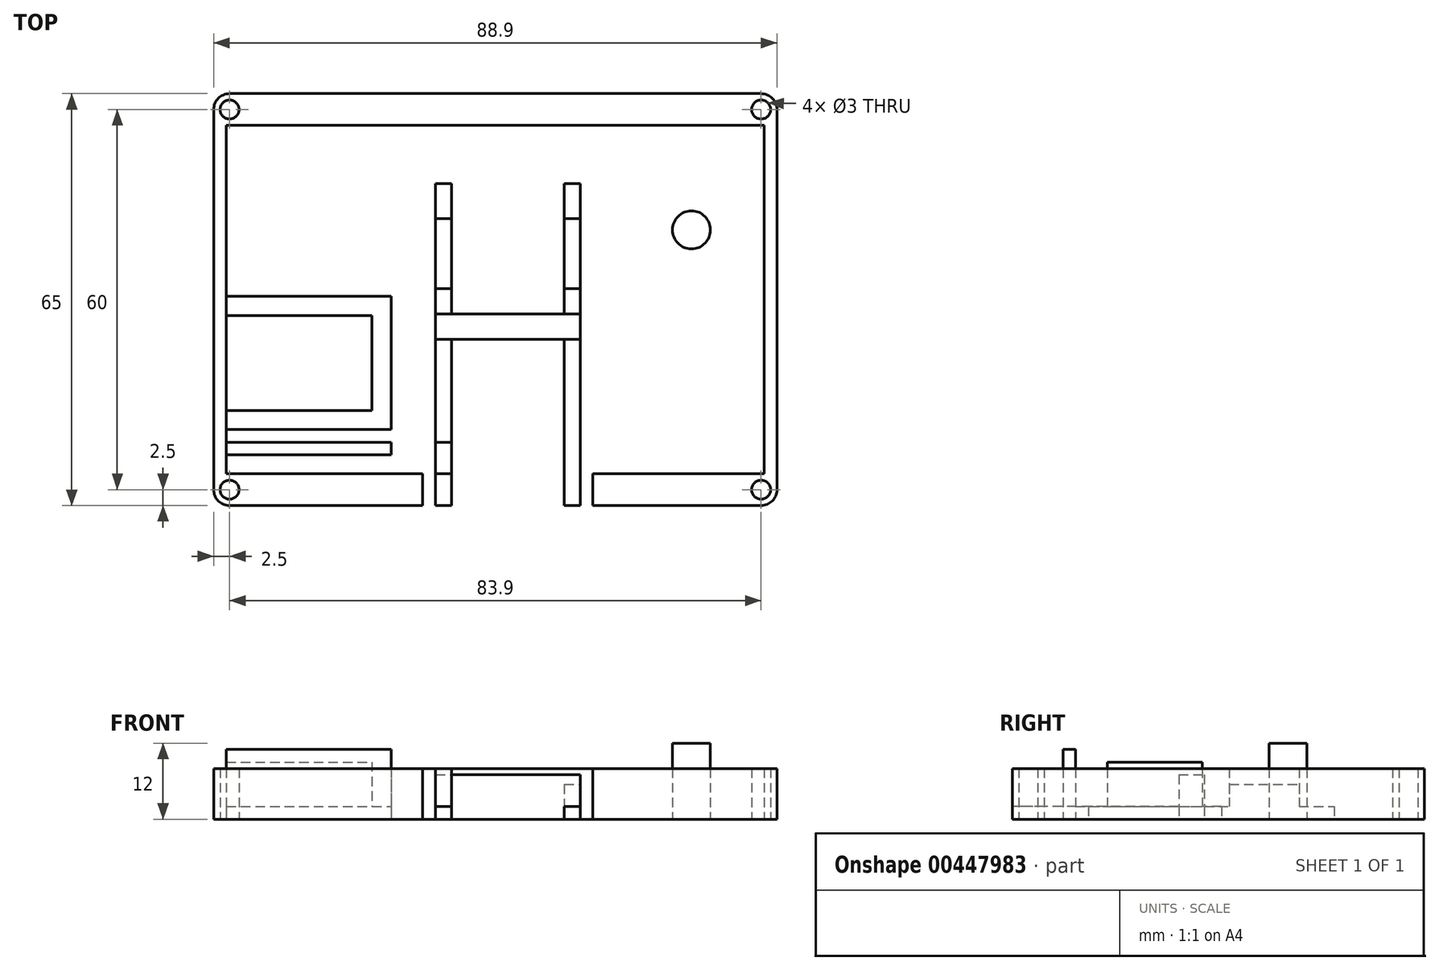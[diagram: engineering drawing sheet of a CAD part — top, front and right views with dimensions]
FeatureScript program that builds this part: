
annotation { "Feature Type Name" : "Feature", "Feature Type Description" : "" }
export const myFeature = defineFeature(function(context is Context, id is Id, definition is map)
    precondition{}
    {
        {
            var Q0;
            Q0=qCreatedBy(makeId("Top.planeOp"),FACE);
            var sketch = newSketch(context, id + "F0", { "sketchPlane" : qUnion([Q0])});
            skLineSegment(sketch, "E0.top", {"start": v(42.45, 27.5) * mm, "end": v(-42.45, 27.5) * mm});
            skLineSegment(sketch, "E0.left", {"start": v(44.45, -27.5) * mm, "end": v(44.45, 27.5) * mm});
            skLineSegment(sketch, "E0.right", {"start": v(-44.45, -27.5) * mm, "end": v(-44.45, 27.5) * mm});
            skPoint(sketch, "E0.middle", {"position": v(0, 0) * mm});
            skLineSegment(sketch, "E1", {"start": v(42.45, 31.41) * mm, "end": v(42.45, 31.27) * mm, "construction": true});
            skLineSegment(sketch, "E2.left", {"start": v(42.45, -20.5) * mm, "end": v(42.45, 0.5) * mm});
            skLineSegment(sketch, "E3.bottom", {"start": v(-42.45, 27.5) * mm, "end": v(42.45, 27.5) * mm});
            skLineSegment(sketch, "E3.top", {"start": v(-41.95, 32.5) * mm, "end": v(41.95, 32.5) * mm});
            skLineSegment(sketch, "E3.left", {"start": v(-44.45, 27.5) * mm, "end": v(-44.45, 30) * mm});
            skLineSegment(sketch, "E3.right", {"start": v(44.45, 27.5) * mm, "end": v(44.45, 30) * mm});
            skLineSegment(sketch, "E4.top", {"start": v(-41.95, -32.5) * mm, "end": v(41.95, -32.5) * mm});
            skLineSegment(sketch, "E4.left", {"start": v(-44.45, -27.5) * mm, "end": v(-44.45, -30) * mm});
            skLineSegment(sketch, "E4.right", {"start": v(44.45, -27.5) * mm, "end": v(44.45, -30) * mm});
            skPoint(sketch, "E5.visualSharp", {"position": v(-44.45, 32.5) * mm});
            skArc(sketch, "E5.filletArc", {"start": v(-41.95, 32.5) * mm, "mid": v(-43.72, 31.77) * mm, "end": v(-44.45, 30) * mm});
            skPoint(sketch, "E6.visualSharp", {"position": v(44.45, 32.5) * mm});
            skArc(sketch, "E6.filletArc", {"start": v(44.45, 30) * mm, "mid": v(43.72, 31.77) * mm, "end": v(41.95, 32.5) * mm});
            skPoint(sketch, "E7.visualSharp", {"position": v(44.45, -32.5) * mm});
            skArc(sketch, "E7.filletArc", {"start": v(41.95, -32.5) * mm, "mid": v(43.72, -31.77) * mm, "end": v(44.45, -30) * mm});
            skPoint(sketch, "E8.visualSharp", {"position": v(-44.45, -32.5) * mm});
            skArc(sketch, "E8.filletArc", {"start": v(-44.45, -30) * mm, "mid": v(-43.72, -31.77) * mm, "end": v(-41.95, -32.5) * mm});
            skCircle(sketch, "E9", {"center": v(-41.95, 30) * mm, "radius": 1.5 * mm});
            skCircle(sketch, "E10", {"center": v(41.95, 30) * mm, "radius": 1.5 * mm});
            skCircle(sketch, "E11", {"center": v(-41.95, -30) * mm, "radius": 1.5 * mm});
            skCircle(sketch, "E12", {"center": v(41.95, -30) * mm, "radius": 1.5 * mm});
            skLineSegment(sketch, "E13.trimOffspring", {"start": v(42.45, 0.5) * mm, "end": v(42.45, -20.5) * mm, "construction": true});
            skLineSegment(sketch, "E14.trimOffspring", {"start": v(42.45, -32.45) * mm, "end": v(42.45, -32.5) * mm, "construction": true});
            skPoint(sketch, "E0.bottom.end.orphan", {"position": v(9.45, -27.5) * mm});
            skLineSegment(sketch, "E15.bottom", {"start": v(-9.45, -32.5) * mm, "end": v(13.41, -32.5) * mm});
            skLineSegment(sketch, "E15.top", {"start": v(-9.45, 18.3) * mm, "end": v(13.4, 18.3) * mm});
            skLineSegment(sketch, "E15.left", {"start": v(-9.45, -32.5) * mm, "end": v(-9.45, 18.3) * mm});
            skLineSegment(sketch, "E15.right", {"start": v(13.41, -32.5) * mm, "end": v(13.4, 18.3) * mm});
            skLineSegment(sketch, "E16.0", {"start": v(10.87, -29.96) * mm, "end": v(10.87, 15.76) * mm});
            skLineSegment(sketch, "E16.1", {"start": v(-6.91, 15.76) * mm, "end": v(10.87, 15.76) * mm, "construction": true});
            skLineSegment(sketch, "E16.2", {"start": v(-6.9, -29.96) * mm, "end": v(-6.91, 15.76) * mm});
            skLineSegment(sketch, "E17", {"start": v(-6.9, -29.96) * mm, "end": v(10.87, -29.96) * mm, "construction": true});
            skLineSegment(sketch, "E18", {"start": v(-42.45, -27.5) * mm, "end": v(-11.45, -27.5) * mm});
            skLineSegment(sketch, "E19", {"start": v(15.41, -27.5) * mm, "end": v(42.45, -27.5) * mm});
            skLineSegment(sketch, "E20", {"start": v(42.45, 27.5) * mm, "end": v(42.45, -27.5) * mm});
            skLineSegment(sketch, "E21", {"start": v(-42.45, 27.5) * mm, "end": v(-42.45, -27.5) * mm});
            skLineSegment(sketch, "E22", {"start": v(-11.45, -27.5) * mm, "end": v(-11.45, -32.5) * mm});
            skLineSegment(sketch, "E23", {"start": v(15.41, -27.5) * mm, "end": v(15.41, -32.5) * mm});
            skPoint(sketch, "E24.MirrorP", {"position": v(30.95, 11) * mm});
            skLineSegment(sketch, "E25.MirrorCS", {"start": v(-42.45, 0.5) * mm, "end": v(-16.45, 0.5) * mm});
            skLineSegment(sketch, "E26.MirrorCS", {"start": v(-16.45, -20.5) * mm, "end": v(-16.45, 0.5) * mm});
            skLineSegment(sketch, "E27.MirrorCS", {"start": v(-42.45, -20.5) * mm, "end": v(-16.45, -20.5) * mm});
            skCircle(sketch, "E28", {"center": v(30.95, 11) * mm, "radius": 3 * mm});
            skLineSegment(sketch, "E29.0", {"start": v(-42.45, -17.5) * mm, "end": v(-19.45, -17.5) * mm});
            skLineSegment(sketch, "E29.1", {"start": v(-19.45, -17.5) * mm, "end": v(-19.45, -2.5) * mm});
            skLineSegment(sketch, "E29.2", {"start": v(-42.45, -2.5) * mm, "end": v(-19.45, -2.5) * mm});
            skLineSegment(sketch, "E30", {"start": v(-42.45, 2.5) * mm, "end": v(-16.5, 2.5) * mm});
            skLineSegment(sketch, "E31", {"start": v(-42.45, -22.5) * mm, "end": v(-16.5, -22.5) * mm});
            skLineSegment(sketch, "E32.bottom", {"start": v(-42.45, -22.5) * mm, "end": v(-16.42, -22.5) * mm});
            skLineSegment(sketch, "E32.top", {"start": v(-42.45, -24.5) * mm, "end": v(-16.42, -24.5) * mm});
            skLineSegment(sketch, "E32.left", {"start": v(-42.45, -22.5) * mm, "end": v(-42.45, -24.5) * mm});
            skLineSegment(sketch, "E32.right", {"start": v(-16.42, -22.5) * mm, "end": v(-16.42, -24.5) * mm});
            skLineSegment(sketch, "E33.left", {"start": v(-42.45, 2.5) * mm, "end": v(-42.45, 2.5) * mm});
            skLineSegment(sketch, "E33.right", {"start": v(-16.5, 2.5) * mm, "end": v(-16.5, 2.5) * mm});
            skLineSegment(sketch, "E34.bottom", {"start": v(-16.5, 2.5) * mm, "end": v(-42.45, 2.5) * mm});
            skLineSegment(sketch, "E34.top", {"start": v(-16.5, 4.5) * mm, "end": v(-42.45, 4.5) * mm});
            skLineSegment(sketch, "E34.left", {"start": v(-16.5, 2.5) * mm, "end": v(-16.5, 4.5) * mm});
            skLineSegment(sketch, "E34.right", {"start": v(-42.45, 2.5) * mm, "end": v(-42.45, 4.5) * mm});
            skLineSegment(sketch, "E35", {"start": v(-9.45, -2.24) * mm, "end": v(13.41, -2.24) * mm});
            skLineSegment(sketch, "E36", {"start": v(-9.45, -6.24) * mm, "end": v(13.41, -6.24) * mm});
            skLineSegment(sketch, "E37", {"start": v(-9.45, 12.76) * mm, "end": v(-6.91, 12.76) * mm});
            skLineSegment(sketch, "E38", {"start": v(-9.45, 1.76) * mm, "end": v(-6.91, 1.76) * mm});
            skLineSegment(sketch, "E39", {"start": v(-9.45, -27.5) * mm, "end": v(-6.9, -27.5) * mm});
            skLineSegment(sketch, "E40", {"start": v(-9.45, -22.5) * mm, "end": v(-6.9, -22.5) * mm});
            skLineSegment(sketch, "E41", {"start": v(-6.9, -22.5) * mm, "end": v(-6.9, -27.5) * mm});
            skLineSegment(sketch, "E42", {"start": v(-6.91, 12.76) * mm, "end": v(-6.91, 1.76) * mm});
            skLineSegment(sketch, "E43", {"start": v(-6.91, 15.76) * mm, "end": v(-6.91, 18.3) * mm});
            skLineSegment(sketch, "E44", {"start": v(10.87, 15.76) * mm, "end": v(10.87, 18.3) * mm});
            skLineSegment(sketch, "E45", {"start": v(-6.9, -29.96) * mm, "end": v(-6.9, -32.5) * mm});
            skLineSegment(sketch, "E46", {"start": v(10.87, -29.96) * mm, "end": v(10.87, -32.5) * mm});
            skLineSegment(sketch, "E47", {"start": v(10.87, 12.76) * mm, "end": v(13.4, 12.76) * mm});
            skLineSegment(sketch, "E48", {"start": v(10.87, 1.76) * mm, "end": v(13.4, 1.76) * mm});
            skLineSegment(sketch, "E49.bottom", {"start": v(-6.91, 18.3) * mm, "end": v(10.87, 18.3) * mm});
            skLineSegment(sketch, "E49.top", {"start": v(-6.91, 18.3) * mm, "end": v(10.87, 18.3) * mm});
            skLineSegment(sketch, "E49.left", {"start": v(-6.91, 18.3) * mm, "end": v(-6.91, 18.3) * mm});
            skLineSegment(sketch, "E49.right", {"start": v(10.87, 18.3) * mm, "end": v(10.87, 18.3) * mm});
            skLineSegment(sketch, "E50.top", {"start": v(-6.91, 19.3) * mm, "end": v(10.87, 19.3) * mm});
            skLineSegment(sketch, "E50.left", {"start": v(-6.91, 18.3) * mm, "end": v(-6.91, 19.3) * mm});
            skLineSegment(sketch, "E50.right", {"start": v(10.87, 18.3) * mm, "end": v(10.87, 19.3) * mm});
            skSolve(sketch);
        }
        {
            var Q0;
            Q0=makeQuery(id+"F0.imprint","IMPRINT",FACE,{"disambiguationData":[TD([[makeQuery(id+"F0.imprint","IMPRINT",EDGE,{"derivedFrom":sQuery(id+"F0.wireOp",EDGE,"b49GfUds-FCf6-TdCI-vDs9-xqUNhDrC5P7H")}),1.0]])]});
            var Q1;
            Q1=makeQuery(id+"F0.imprint","IMPRINT",FACE,{"disambiguationData":[TD([[makeQuery(id+"F0.imprint","IMPRINT",EDGE,{"derivedFrom":sQuery(id+"F0.wireOp",EDGE,"zLugwVok-1eod-zGnS-IKgy-gRwgS7il9mY1")}),1.0]])]});
            var Q2;
            Q2=makeQuery(id+"F0.imprint","IMPRINT",FACE,{"disambiguationData":[TD([[makeQuery(id+"F0.imprint","IMPRINT",EDGE,{"derivedFrom":sQuery(id+"F0.wireOp",EDGE,"gfQSOBsQ-dL06-kA9A-z0KN-fCnpzNCFb0XH")}),1.0]])]});
            var Q3;
            Q3=makeQuery(id+"F0.imprint","IMPRINT",FACE,{"disambiguationData":[TD([[makeQuery(id+"F0.imprint","IMPRINT",EDGE,{"derivedFrom":sQuery(id+"F0.wireOp",EDGE,"Z4DMVKM8-imfN-ioXY-uNkh-o1IQfbVLOKmH")}),1.0]])]});
            var Q4;
            Q4=makeQuery(id+"F0.imprint","IMPRINT",FACE,{"disambiguationData":[TD([[makeQuery(id+"F0.imprint","IMPRINT",EDGE,{"derivedFrom":sQuery(id+"F0.wireOp",EDGE,"E0.left")}),1.0]])]});
            var Q5;
            {var subQ0=sQuery(id+"F0.wireOp",EDGE,"5yO6ONQU-jHeC-KW85-spt1-Q7ioaqvRXlnz");Q5=makeQuery(id+"F0.imprint","IMPRINT",FACE,{"disambiguationData":[TD([[makeQuery(id+"F0.imprint","IMPRINT",EDGE,{"derivedFrom":subQ0}),-1.0]])]});}
            var Q6;
            {var subQ0=sQuery(id+"F0.wireOp",EDGE,"J2lE2n3h-ec9A-8HLJ-wN6o-8rqhVOWuaEZe");Q6=makeQuery(id+"F0.imprint","IMPRINT",FACE,{"disambiguationData":[TD([[makeQuery(id+"F0.imprint","IMPRINT",EDGE,{"derivedFrom":subQ0}),-1.0]])]});}
            var Q7;
            {var subQ0=sQuery(id+"F0.wireOp",EDGE,"E37");Q7=makeQuery(id+"F0.imprint","IMPRINT",FACE,{"disambiguationData":[TD([[makeQuery(id+"F0.imprint","IMPRINT",EDGE,{"derivedFrom":subQ0}),-1.0]])]});}
            var Q8;
            {var subQ0=sQuery(id+"F0.wireOp",EDGE,"E39");Q8=makeQuery(id+"F0.imprint","IMPRINT",FACE,{"disambiguationData":[TD([[makeQuery(id+"F0.imprint","IMPRINT",EDGE,{"derivedFrom":subQ0}),1.0]])]});}
            extrude(context, id + "F1", {"entities" : qUnion([Q0, Q1, Q2, Q3, Q4, Q5, Q6, Q7, Q8]), "depth" : 8 * mm});
        }
        {
            var Q0;
            {var subQ3=sQuery(id+"F0.wireOp",EDGE,"E3.bottom");Q0=makeQuery(id+"F0.imprint","IMPRINT",FACE,{"disambiguationData":[TD([[makeQuery(id+"F0.imprint","IMPRINT",EDGE,{"derivedFrom":subQ3}),-1.0]])]});}
            var Q1;
            {var subQ0=sQuery(id+"F0.wireOp",EDGE,"E25.MirrorCS");Q1=makeQuery(id+"F0.imprint","IMPRINT",FACE,{"disambiguationData":[TD([[makeQuery(id+"F0.imprint","IMPRINT",EDGE,{"derivedFrom":subQ0}),-1.0]])]});}
            var Q2;
            {var subQ3=sQuery(id+"F0.wireOp",EDGE,"E40");Q2=makeQuery(id+"F0.imprint","IMPRINT",FACE,{"disambiguationData":[TD([[makeQuery(id+"F0.imprint","IMPRINT",EDGE,{"derivedFrom":subQ3}),1.0]])]});}
            var Q3;
            {var subQ0=sQuery(id+"F0.wireOp",EDGE,"E35");var subQ1=sQuery(id+"F0.wireOp",EDGE,"E15.left");var subQ2=makeQuery(id+"F0.imprint","INTERSECT",VERTEX,{"derivedFrom":[subQ1,subQ0]});Q3=makeQuery(id+"F0.imprint","IMPRINT",FACE,{"disambiguationData":[TD([[makeQuery(id+"F0.imprint","IMPRINT",EDGE,{"disambiguationData":[TD([[subQ2,1.0]])],"derivedFrom":subQ1}),-1.0]])]});}
            var Q4;
            {var subQ3=sQuery(id+"F0.wireOp",EDGE,"E38");Q4=makeQuery(id+"F0.imprint","IMPRINT",FACE,{"disambiguationData":[TD([[makeQuery(id+"F0.imprint","IMPRINT",EDGE,{"derivedFrom":subQ3}),-1.0]])]});}
            var Q5;
            {var subQ0=sQuery(id+"F0.wireOp",EDGE,"E37");Q5=makeQuery(id+"F0.imprint","IMPRINT",FACE,{"disambiguationData":[TD([[makeQuery(id+"F0.imprint","IMPRINT",EDGE,{"derivedFrom":subQ0}),1.0]])]});}
            var Q6;
            {var subQ0=sQuery(id+"F0.wireOp",EDGE,"E39");Q6=makeQuery(id+"F0.imprint","IMPRINT",FACE,{"disambiguationData":[TD([[makeQuery(id+"F0.imprint","IMPRINT",EDGE,{"derivedFrom":subQ0}),-1.0]])]});}
            var Q7;
            {var subQ5=sQuery(id+"F0.wireOp",EDGE,"E46");Q7=makeQuery(id+"F0.imprint","IMPRINT",FACE,{"disambiguationData":[TD([[makeQuery(id+"F0.imprint","IMPRINT",EDGE,{"derivedFrom":subQ5}),1.0]])]});}
            var Q8;
            {var subQ0=sQuery(id+"F0.wireOp",EDGE,"E35");var subQ1=sQuery(id+"F0.wireOp",EDGE,"E15.right");var subQ2=makeQuery(id+"F0.imprint","INTERSECT",VERTEX,{"derivedFrom":[subQ1,subQ0]});Q8=makeQuery(id+"F0.imprint","IMPRINT",FACE,{"disambiguationData":[TD([[makeQuery(id+"F0.imprint","IMPRINT",EDGE,{"disambiguationData":[TD([[subQ2,1.0]])],"derivedFrom":subQ1}),1.0]])]});}
            var Q9;
            {var subQ5=sQuery(id+"F0.wireOp",EDGE,"E44");Q9=makeQuery(id+"F0.imprint","IMPRINT",FACE,{"disambiguationData":[TD([[makeQuery(id+"F0.imprint","IMPRINT",EDGE,{"derivedFrom":subQ5}),-1.0]])]});}
            var Q10;
            {var subQ3=sQuery(id+"F0.wireOp",EDGE,"E48");Q10=makeQuery(id+"F0.imprint","IMPRINT",FACE,{"disambiguationData":[TD([[makeQuery(id+"F0.imprint","IMPRINT",EDGE,{"derivedFrom":subQ3}),-1.0]])]});}
            extrude(context, id + "F2", {"entities" : qUnion([Q0, Q1, Q2, Q3, Q4, Q5, Q6, Q7, Q8, Q9, Q10]), "operationType" : NewBodyOperationType.ADD, "depth" : 2 * mm});
        }
        {
            var Q0;
            {var subQ0=sQuery(id+"F0.wireOp",EDGE,"E29.0");Q0=makeQuery(id+"F0.imprint","IMPRINT",FACE,{"disambiguationData":[TD([[makeQuery(id+"F0.imprint","IMPRINT",EDGE,{"derivedFrom":subQ0}),1.0]])]});}
            extrude(context, id + "F3", {"entities" : qUnion([Q0]), "operationType" : NewBodyOperationType.ADD, "depth" : 9 * mm});
        }
        {
            var Q0;
            Q0=makeQuery(id+"F0.imprint","IMPRINT",FACE,{"disambiguationData":[TD([[makeQuery(id+"F0.imprint","IMPRINT",EDGE,{"derivedFrom":sQuery(id+"F0.wireOp",EDGE,"E34.bottom")}),-1.0]])]});
            var Q1;
            Q1=makeQuery(id+"F0.imprint","IMPRINT",FACE,{"disambiguationData":[TD([[makeQuery(id+"F0.imprint","IMPRINT",EDGE,{"derivedFrom":sQuery(id+"F0.wireOp",EDGE,"E32.top")}),1.0]])]});
            extrude(context, id + "F4", {"entities" : qUnion([Q0, Q1]), "operationType" : NewBodyOperationType.ADD, "depth" : 11 * mm});
        }
        {
            var Q0;
            {var subQ0=sQuery(id+"F0.wireOp",EDGE,"E36");var subQ1=sQuery(id+"F0.wireOp",EDGE,"E16.0");var subQ2=makeQuery(id+"F0.imprint","INTERSECT",VERTEX,{"derivedFrom":[subQ1,subQ0]});Q0=makeQuery(id+"F0.imprint","IMPRINT",FACE,{"disambiguationData":[TD([[makeQuery(id+"F0.imprint","IMPRINT",EDGE,{"disambiguationData":[TD([[subQ2,-1.0]])],"derivedFrom":subQ1}),1.0]])]});}
            var Q1;
            {var subQ0=sQuery(id+"F0.wireOp",EDGE,"E35");var subQ1=sQuery(id+"F0.wireOp",EDGE,"E15.right");var subQ2=makeQuery(id+"F0.imprint","INTERSECT",VERTEX,{"derivedFrom":[subQ1,subQ0]});Q1=makeQuery(id+"F0.imprint","IMPRINT",FACE,{"disambiguationData":[TD([[makeQuery(id+"F0.imprint","IMPRINT",EDGE,{"disambiguationData":[TD([[subQ2,1.0]])],"derivedFrom":subQ1}),1.0]])]});}
            var Q2;
            {var subQ0=sQuery(id+"F0.wireOp",EDGE,"E35");var subQ1=sQuery(id+"F0.wireOp",EDGE,"E15.left");var subQ2=makeQuery(id+"F0.imprint","INTERSECT",VERTEX,{"derivedFrom":[subQ1,subQ0]});Q2=makeQuery(id+"F0.imprint","IMPRINT",FACE,{"disambiguationData":[TD([[makeQuery(id+"F0.imprint","IMPRINT",EDGE,{"disambiguationData":[TD([[subQ2,1.0]])],"derivedFrom":subQ1}),-1.0]])]});}
            extrude(context, id + "F5", {"entities" : qUnion([Q0, Q1, Q2]), "operationType" : NewBodyOperationType.ADD, "depth" : 7 * mm});
        }
        {
            var Q0;
            {var subQ0=sQuery(id+"F0.wireOp",EDGE,"E47");Q0=makeQuery(id+"F0.imprint","IMPRINT",FACE,{"disambiguationData":[TD([[makeQuery(id+"F0.imprint","IMPRINT",EDGE,{"derivedFrom":subQ0}),-1.0]])]});}
            extrude(context, id + "F6", {"entities" : qUnion([Q0]), "operationType" : NewBodyOperationType.ADD, "depth" : 5.5 * mm});
        }
        {
            var Q0;
            Q0=makeQuery(id+"F0.imprint","IMPRINT",FACE,{"disambiguationData":[TD([[makeQuery(id+"F0.imprint","IMPRINT",EDGE,{"derivedFrom":sQuery(id+"F0.wireOp",EDGE,"E28")}),1.0]])]});
            extrude(context, id + "F7", {"entities" : qUnion([Q0]), "operationType" : NewBodyOperationType.ADD, "depth" : 12 * mm});
        }
    });
